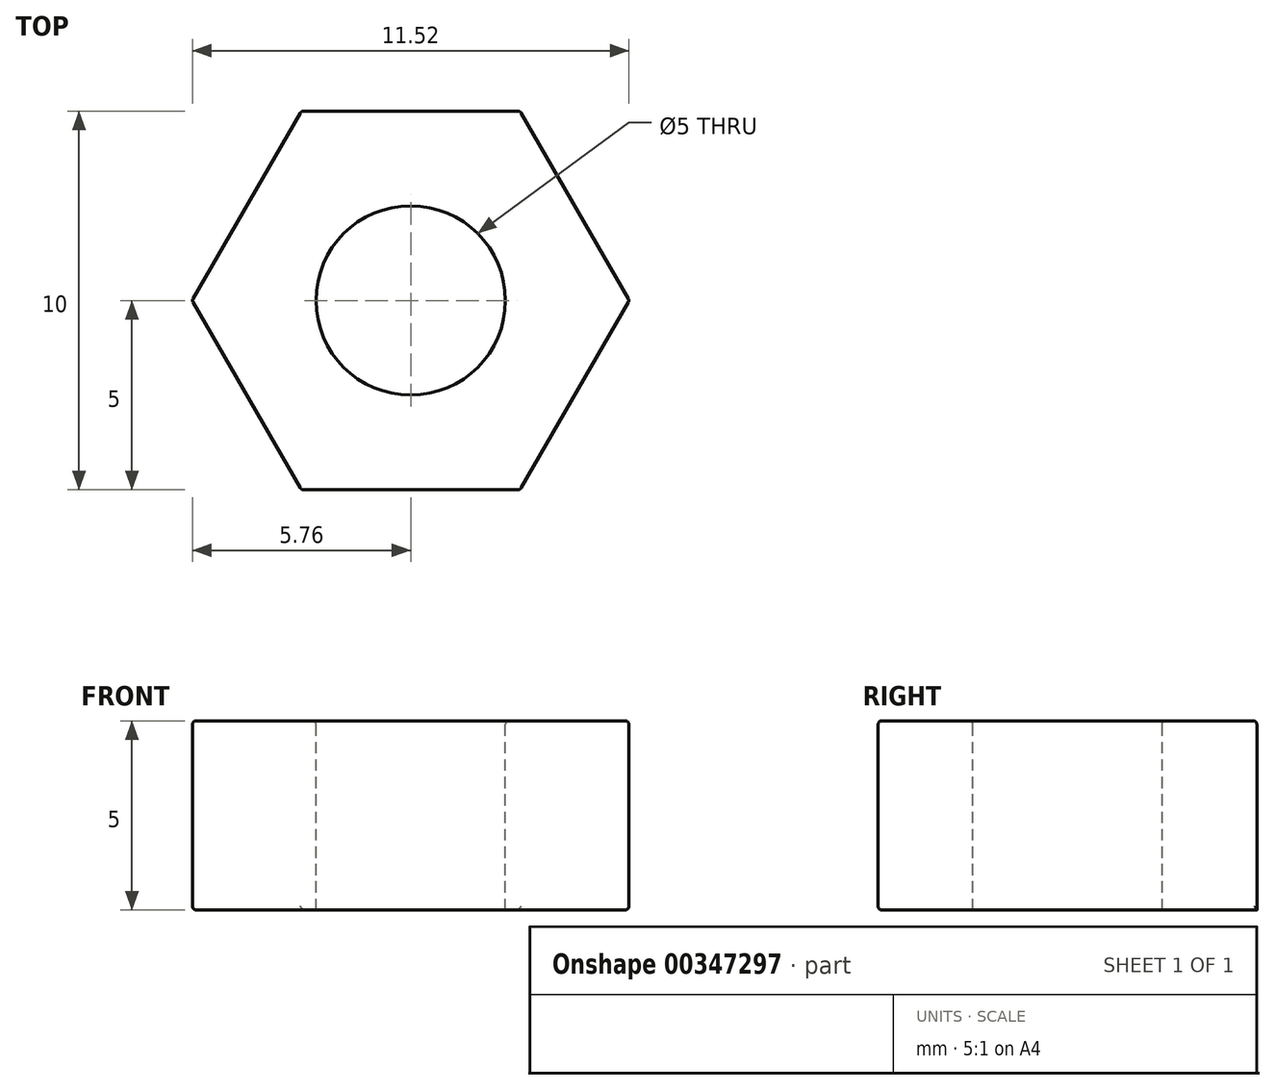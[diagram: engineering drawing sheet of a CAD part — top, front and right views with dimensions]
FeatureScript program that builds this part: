
annotation { "Feature Type Name" : "Feature", "Feature Type Description" : "" }
export const myFeature = defineFeature(function(context is Context, id is Id, definition is map)
    precondition{}
    {
        {
            var Q0;
            Q0=qCreatedBy(makeId("Top.planeOp"),FACE);
            var sketch = newSketch(context, id + "F0", { "sketchPlane" : qUnion([Q0])});
            skCircle(sketch, "E0.cCircle", {"center": v(0, 0) * mm, "radius": 5 * mm, "construction": true});
            skLineSegment(sketch, "E0.0", {"start": v(5.77, 0) * mm, "end": v(2.89, -5) * mm});
            skLineSegment(sketch, "E0.1", {"start": v(2.89, -5) * mm, "end": v(-2.89, -5) * mm});
            skLineSegment(sketch, "E0.2", {"start": v(-2.89, -5) * mm, "end": v(-5.77, 0) * mm});
            skLineSegment(sketch, "E0.3", {"start": v(-5.77, 0) * mm, "end": v(-2.89, 5) * mm});
            skLineSegment(sketch, "E0.4", {"start": v(-2.89, 5) * mm, "end": v(2.89, 5) * mm});
            skLineSegment(sketch, "E0.5", {"start": v(2.89, 5) * mm, "end": v(5.77, 0) * mm});
            skPoint(sketch, "E0.0.midPoint", {"position": v(4.33, -2.5) * mm});
            skCircle(sketch, "E1", {"center": v(0, 0) * mm, "radius": 2.5 * mm});
            skSolve(sketch);
        }
        {
            var Q0;
            Q0 = qSketchRegion(id + "F0", true);
            extrude(context, id + "F1", {"entities" : qUnion([Q0]), "oppositeDirection" : true, "depth" : 5 * mm});
        }
        {
            var Q0;
            Q0=makeQuery(id+"F1.opExtrude","CAP_EDGE",EDGE,{"disambiguationData":[OSD([sQuery(id+"F0.wireOp",EDGE,"E0.0")])],"isStart":false});
            var Q1;
            Q1=makeQuery(id+"F1.opExtrude","SWEPT_EDGE",EDGE,{"disambiguationData":[OSD([sQuery(id+"F0.wireOp",EDGE,"E0.0"),sQuery(id+"F0.wireOp",EDGE,"E0.5")])]});
            var Q2;
            Q2=makeQuery(id+"F1.opExtrude","CAP_EDGE",EDGE,{"disambiguationData":[OSD([sQuery(id+"F0.wireOp",EDGE,"E0.5")])],"isStart":false});
            var Q3;
            Q3=makeQuery(id+"F1.opExtrude","CAP_EDGE",EDGE,{"disambiguationData":[OSD([sQuery(id+"F0.wireOp",EDGE,"E0.1")])],"isStart":false});
            var Q4;
            Q4=makeQuery(id+"F1.opExtrude","CAP_FACE",FACE,{"disambiguationData":[OSD([sQuery(id+"F0.wireOp",EDGE,"E0.0"),sQuery(id+"F0.wireOp",EDGE,"E0.1"),sQuery(id+"F0.wireOp",EDGE,"E0.2"),sQuery(id+"F0.wireOp",EDGE,"E0.3"),sQuery(id+"F0.wireOp",EDGE,"E0.4"),sQuery(id+"F0.wireOp",EDGE,"E0.5"),sQuery(id+"F0.wireOp",EDGE,"E1")])],"isStart":true});
            var Q5;
            Q5=makeQuery(id+"F1.opExtrude","SWEPT_FACE",FACE,{"disambiguationData":[OSD([sQuery(id+"F0.wireOp",EDGE,"E0.0")])]});
            var Q6;
            Q6=makeQuery(id+"F1.opExtrude","SWEPT_FACE",FACE,{"disambiguationData":[OSD([sQuery(id+"F0.wireOp",EDGE,"E0.1")])]});
            var Q7;
            Q7=makeQuery(id+"F1.opExtrude","SWEPT_EDGE",EDGE,{"disambiguationData":[OSD([sQuery(id+"F0.wireOp",EDGE,"E0.4"),sQuery(id+"F0.wireOp",EDGE,"E0.5")])]});
            var Q8;
            Q8=makeQuery(id+"F1.opExtrude","SWEPT_FACE",FACE,{"disambiguationData":[OSD([sQuery(id+"F0.wireOp",EDGE,"E0.3")])]});
            var Q9;
            Q9=makeQuery(id+"F1.opExtrude","SWEPT_FACE",FACE,{"disambiguationData":[OSD([sQuery(id+"F0.wireOp",EDGE,"E0.2")])]});
            fillet(context, id + "F2", {"entities" : qUnion([Q0, Q1, Q2, Q3, Q4, Q5, Q6, Q7, Q8, Q9]), "radius" : 0.1 * mm, "tangentPropagation" : true, "allowEdgeOverflow" : false});
        }
    });
